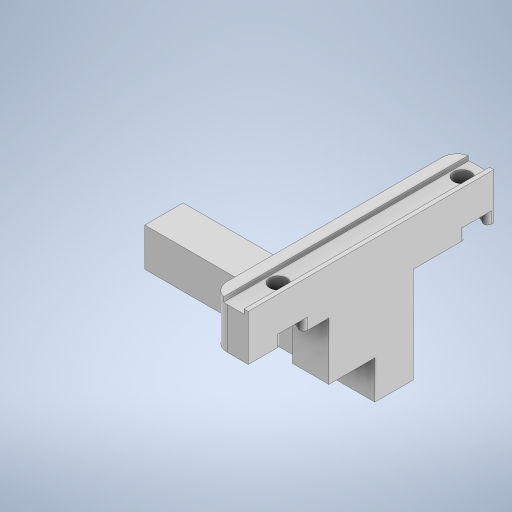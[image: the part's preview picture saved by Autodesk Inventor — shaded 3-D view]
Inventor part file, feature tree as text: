
AUTODESK INVENTOR PART (.ipt)
format: ipt  version: 2024 (Build 280153000, 153)  size: 314,368 bytes
history: native  units: in
note: dims shown in document units (in); Inventor stores cm internally (conversion verified against a paired STEP export)
features: extrude x5, sketch x5, projected_geometry x4, fillet x2
ambient origin geometry x8: Origin, YZ Plane, XZ Plane, XY Plane, X Axis, Y Axis, Z Axis, Center Point
bodies: Solid1 (feature_tree)
feature tree (16):
  extrude  "Extrusion1"  Depth=2.5197in
  extrude  "Extrusion2"  Depth=1.8898in
  extrude  "Extrusion3"  Depth=0.4724in TaperAngle=0.0deg
  fillet  "Fillet1"  Radius=0.0433in
  fillet  "Fillet2"  Radius=0.2126in
  extrude  "Extrusion15"  Depth=0.4724in TaperAngle=0.0deg
  extrude  "Extrusion16"  Depth=0.1181in TaperAngle=0.0deg
  sketch  "Sketch1"  dims[d1=0.374in d2=2.5197in]
  sketch  "Sketch2"  dims[d3=0.1772in d4=1.8898in]
  sketch  "Sketch3"  dims[d6=0.1457in d7=0.4724in d8=0.0in d9=0.0433in d10=0.2126in]
  projected_geometry  "Projected Loop2"
  projected_geometry  "Projected Loop3"
  projected_geometry  "Projected Loop4"
  projected_geometry  "Projected Loop5"
  sketch  "Sketch15"  dims[d11=0.0472in d12=0.4724in d13=0.0in]
  sketch  "Sketch16"  dims[d14=0.2953in d15=0.1181in d16=0.0in d17=0.1772in d18=0.0394in d19=0.1575in d76=0.4724in d79=0.4331in d80=0.8661in d81=0.5906in d82=0.0in d83=2.3622in d84=0.3937in d85=2.3622in d86=0.3937in d87=0.0in d42=0.0197in d43=0.0344in d44=0.0197in d45=0.0344in d46=0.0in d47=0.0in d48=0.0in d49=0.0in d50=0.0in d51=0.0in d52=0.0in d53=0.0in d55=0.0197in d56=0.0344in d57=0.0197in d58=0.0344in d60=0.0197in d61=0.0344in d62=0.0197in d63=0.0344in d72=0.0197in d73=0.0344in d74=0.0197in d75=0.0344in]
